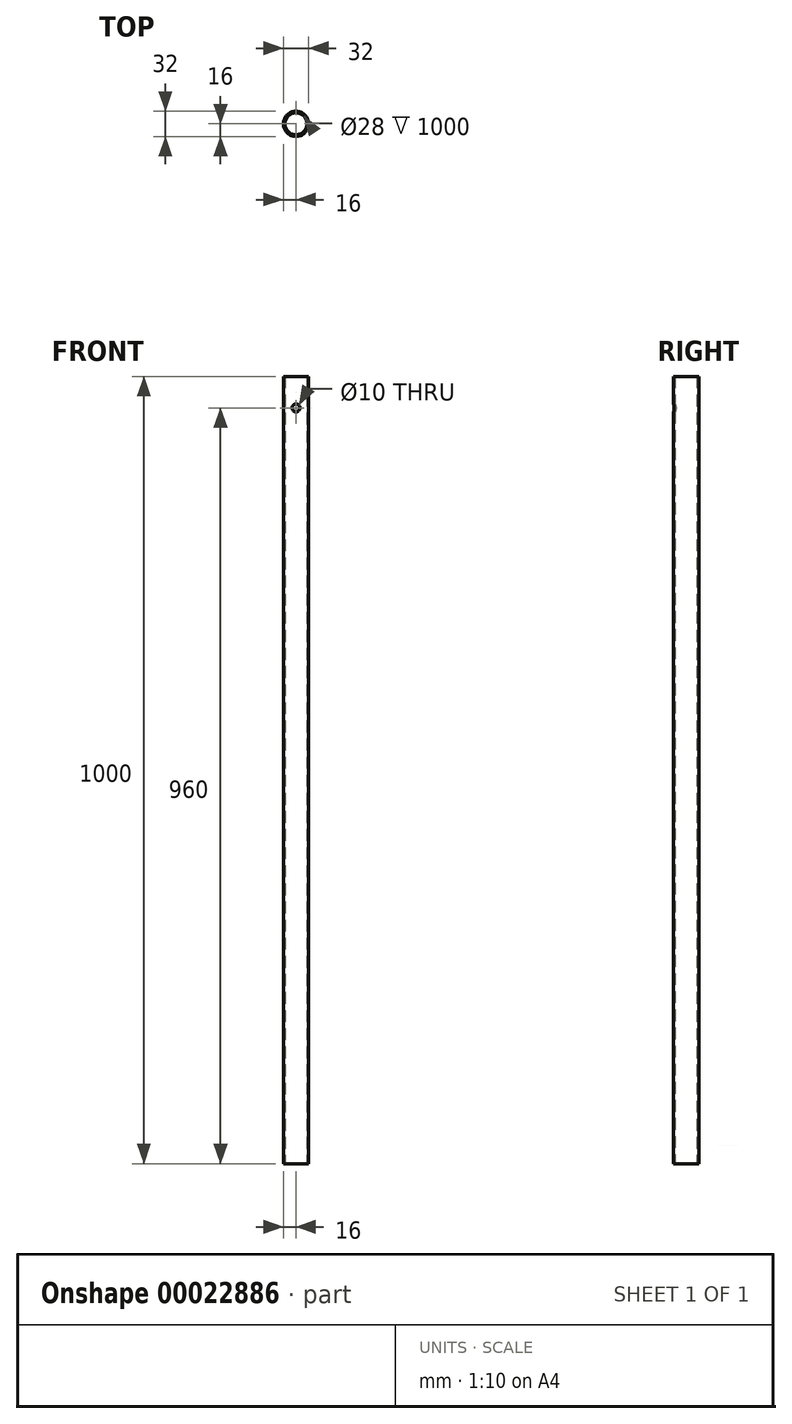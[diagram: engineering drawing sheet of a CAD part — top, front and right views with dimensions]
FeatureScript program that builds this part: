
annotation { "Feature Type Name" : "Feature", "Feature Type Description" : "" }
export const myFeature = defineFeature(function(context is Context, id is Id, definition is map)
    precondition{}
    {
        {
            var Q0;
            Q0=qCreatedBy(makeId("Top.planeOp"),FACE);
            var sketch = newSketch(context, id + "F0", { "sketchPlane" : qUnion([Q0])});
            skCircle(sketch, "E0", {"center": v(0, 0) * mm, "radius": 16 * mm});
            skCircle(sketch, "E1", {"center": v(0, 0) * mm, "radius": 14 * mm});
            skSolve(sketch);
        }
        {
            var Q0;
            Q0=makeQuery(id+"F0.imprint","IMPRINT",FACE,{"disambiguationData":[TD([[makeQuery(id+"F0.imprint","IMPRINT",EDGE,{"derivedFrom":sQuery(id+"F0.wireOp",EDGE,"E0")}),1.0]])]});
            extrude(context, id + "F1", {"entities" : qUnion([Q0]), "depth" : 1000 * mm});
        }
        {
            var Q0;
            Q0=qCreatedBy(makeId("Front.planeOp"),FACE);
            var sketch = newSketch(context, id + "F2", { "sketchPlane" : qUnion([Q0])});
            skPoint(sketch, "E2", {"position": v(0, 960) * mm});
            skSolve(sketch);
        }
        {
            var Q0;
            Q0=sQuery(id+"F2.wireOp",VERTEX,"E2");
            var Q1;
            Q1=makeQuery(id+"F1.opExtrude","SWEPT_BODY",BODY,{"disambiguationData":[OSD([sQuery(id+"F0.wireOp",EDGE,"E0"),sQuery(id+"F0.wireOp",EDGE,"E1")])]});
            hole(context, id + "F3", {"style" : HoleStyle.SIMPLE, "holeDiameter" : 10 * mm, "endStyle" : HoleEndStyle.THROUGH, "oppositeDirection" : true, "locations" : qUnion([Q0]), "scope" : qUnion([Q1])});
        }
    });
